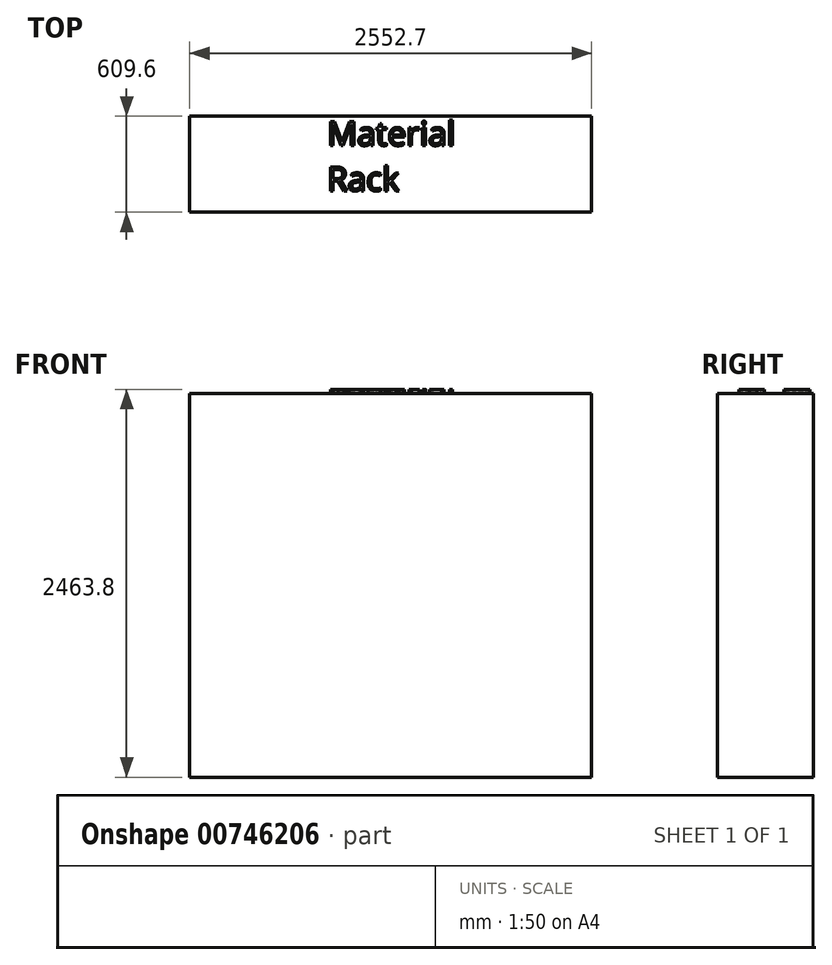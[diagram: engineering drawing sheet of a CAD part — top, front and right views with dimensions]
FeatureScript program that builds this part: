
annotation { "Feature Type Name" : "Feature", "Feature Type Description" : "" }
export const myFeature = defineFeature(function(context is Context, id is Id, definition is map)
    precondition{}
    {
        {
            var Q0;
            Q0=qCreatedBy(makeId("Front.planeOp"),FACE);
            var sketch = newSketch(context, id + "F0", { "sketchPlane" : qUnion([Q0])});
            skLineSegment(sketch, "E0.bottom", {"start": v(1276.35, -1219.2) * mm, "end": v(-1276.35, -1219.2) * mm});
            skLineSegment(sketch, "E0.top", {"start": v(1276.35, 1219.2) * mm, "end": v(-1276.35, 1219.2) * mm});
            skLineSegment(sketch, "E0.left", {"start": v(1276.35, -1219.2) * mm, "end": v(1276.35, 1219.2) * mm});
            skLineSegment(sketch, "E0.right", {"start": v(-1276.35, -1219.2) * mm, "end": v(-1276.35, 1219.2) * mm});
            skPoint(sketch, "E0.middle", {"position": v(0, 0) * mm});
            skSolve(sketch);
        }
        {
            var Q0;
            Q0 = qSketchRegion(id + "F0", true);
            extrude(context, id + "F1", {"entities" : qUnion([Q0]), "depth" : 609.6 * mm, "offsetDistance" : 25.4 * mm});
        }
        {
            var Q0;
            Q0=makeQuery(id+"F1.opExtrude","SWEPT_FACE",FACE,{"disambiguationData":[OSD([sQuery(id+"F0.wireOp",EDGE,"E0.top")])]});
            var sketch = newSketch(context, id + "F2", { "sketchPlane" : qUnion([Q0])});
            skText(sketch, "E1", { "text": "Material\nRack", "fontName": "OpenSans-Regular.ttf"});
            const initialGuessF2  = {"E1": [-0.40451, -0.18584, 1, 0, 0.1524]};
            skSetInitialGuess(sketch, initialGuessF2);
            skSolve(sketch);
        }
        {
            var Q0;
            Q0 = qSketchRegion(id + "F2", true);
            extrude(context, id + "F3", {"entities" : qUnion([Q0]), "operationType" : NewBodyOperationType.ADD, "depth" : 25.4 * mm, "offsetDistance" : 25.4 * mm});
        }
    });
